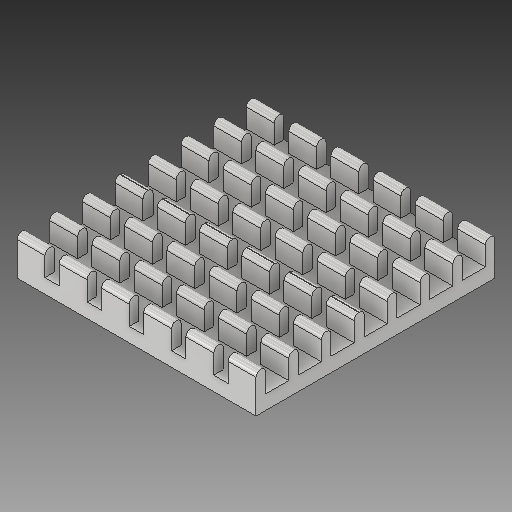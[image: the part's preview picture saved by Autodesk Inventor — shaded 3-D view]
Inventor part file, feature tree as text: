
AUTODESK INVENTOR PART (.ipt)
format: ipt  version: 2019.3 (Build 233278000, 278)  size: 389,632 bytes
history: native  units: mm
features: extrude x3, sketch x3, fillet x1
ambient origin geometry x8: Origin, YZ Plane, XZ Plane, XY Plane, X Axis, Y Axis, Z Axis, Center Point
bodies: Solid1 (feature_tree)
feature tree (7):
  extrude  "Extrusion1"  Depth=25.0mm
  extrude  "Extrusion4"  Depth=1.0mm
  fillet  "Fillet1"  Radius=2.42mm
  extrude  "Extrusion5"  Depth=1.0mm
  sketch  "Sketch1"  dims[d0=25.0mm d1=25.0mm]
  sketch  "Sketch2"  dims[d2=4.0mm d3=0.0mm d5=1.0mm d6=2.42mm]
  sketch  "Sketch3"  dims[d7=2.42mm d8=1.0mm d9=2.42mm d10=1.0mm d12=1.5mm d13=2.42mm d14=1.0mm d22=10.0mm d23=0.0mm d24=0.5mm d25=2.9167mm d26=1.5mm d27=1.5mm d28=50.0mm d30=4.4167mm d31=10.0mm d33=10.0mm d35=2.9165mm d36=10.0mm d37=0.0mm]
